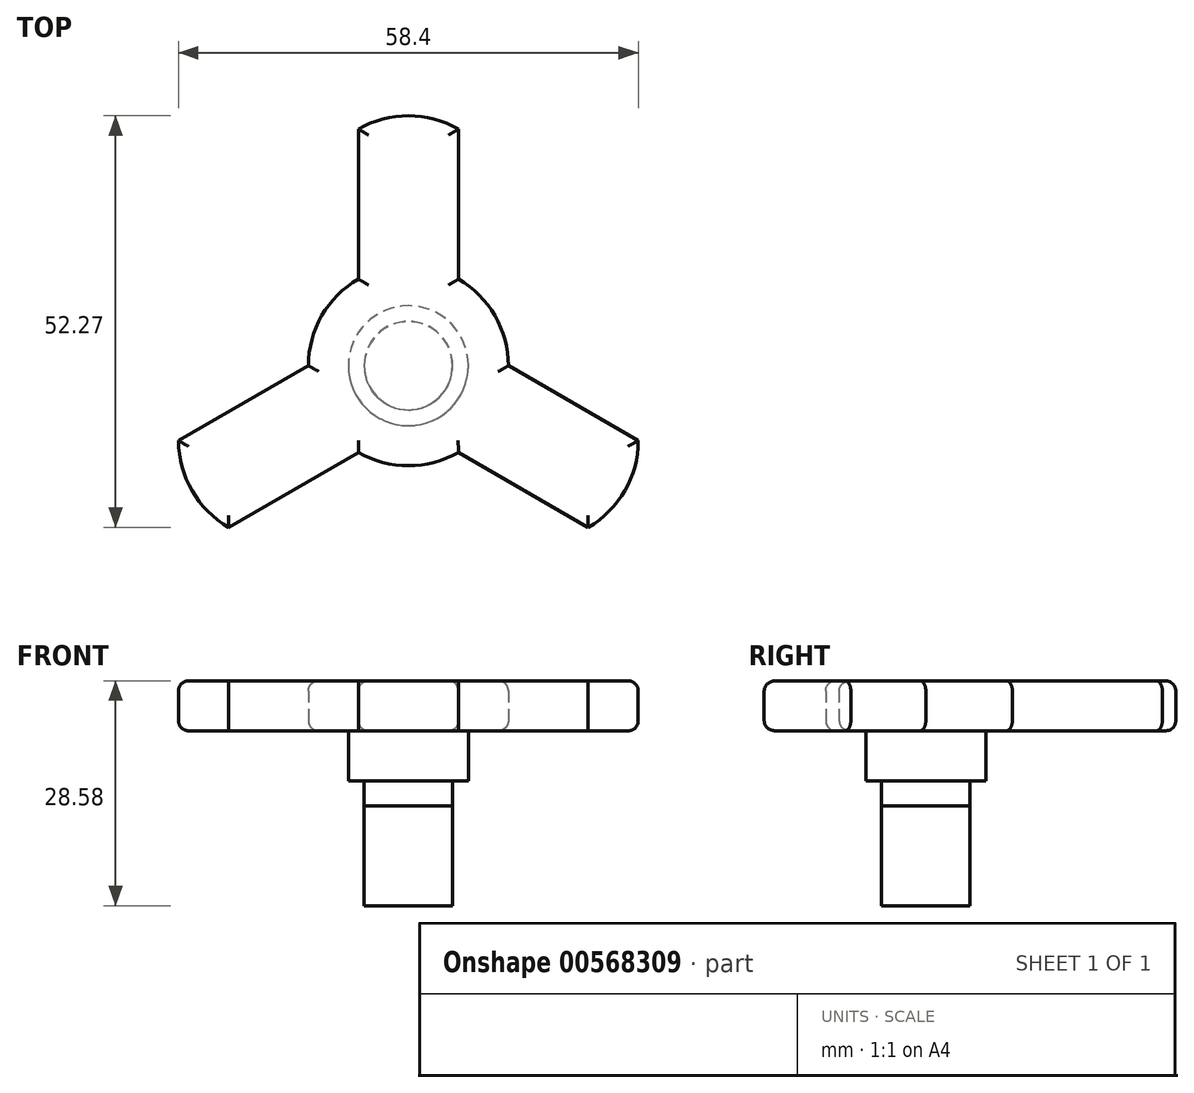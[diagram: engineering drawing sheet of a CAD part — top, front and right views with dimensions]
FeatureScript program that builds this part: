
annotation { "Feature Type Name" : "Feature", "Feature Type Description" : "" }
export const myFeature = defineFeature(function(context is Context, id is Id, definition is map)
    precondition{}
    {
        {
            var Q0;
            Q0=qCreatedBy(makeId("Top.planeOp"),FACE);
            var sketch = newSketch(context, id + "F0", { "sketchPlane" : qUnion([Q0])});
            skCircle(sketch, "E0", {"center": v(0, 0) * mm, "radius": 5.63 * mm});
            skSolve(sketch);
        }
        {
            var Q0;
            Q0 = qSketchRegion(id + "F0", true);
            extrude(context, id + "F1", {"entities" : qUnion([Q0]), "depth" : 12.7 * mm, "offsetDistance" : 25.4 * mm});
        }
        {
            var Q0;
            Q0=makeQuery(id+"F1.opExtrude","CAP_FACE",FACE,{"disambiguationData":[OSD([sQuery(id+"F0.wireOp",EDGE,"E0")])],"isStart":false});
            var sketch = newSketch(context, id + "F2", { "sketchPlane" : qUnion([Q0])});
            skCircle(sketch, "E1", {"center": v(0, 0) * mm, "radius": 5.6 * mm});
            skSolve(sketch);
        }
        {
            var Q0;
            Q0 = qSketchRegion(id + "F2", true);
            extrude(context, id + "F3", {"entities" : qUnion([Q0]), "operationType" : NewBodyOperationType.ADD, "depth" : 9.52 * mm, "offsetDistance" : 25.4 * mm});
        }
        {
            var Q0;
            Q0=makeQuery(id+"F3.opExtrude","CAP_FACE",FACE,{"disambiguationData":[OSD([sQuery(id+"F2.wireOp",EDGE,"E1")])],"isStart":false});
            var sketch = newSketch(context, id + "F4", { "sketchPlane" : qUnion([Q0])});
            skCircle(sketch, "E2", {"center": v(0, 0) * mm, "radius": 12.7 * mm});
            skSolve(sketch);
        }
        {
            var Q0;
            Q0=makeQuery(id+"F4.imprint","IMPRINT",FACE,{"disambiguationData":[TD([[makeQuery(id+"F4.imprint","IMPRINT",EDGE,{"derivedFrom":sQuery(id+"F4.wireOp",EDGE,"E2")}),1.0]])]});
            var sketch = newSketch(context, id + "F5", { "sketchPlane" : qUnion([Q0])});
            skLineSegment(sketch, "E3.left", {"start": v(-6.35, 11) * mm, "end": v(-6.35, 30.05) * mm});
            skLineSegment(sketch, "E3.right", {"start": v(6.35, 11) * mm, "end": v(6.35, 30.05) * mm});
            skLineSegment(sketch, "E4.1.0", {"start": v(-12.7, 0) * mm, "end": v(-29.2, -9.52) * mm});
            skLineSegment(sketch, "E4.2.0", {"start": v(6.35, -11) * mm, "end": v(22.85, -20.52) * mm});
            skPoint(sketch, "E4.center", {"position": v(0, 0) * mm});
            skLineSegment(sketch, "E5.1.0", {"start": v(-6.35, -11) * mm, "end": v(-22.85, -20.52) * mm});
            skLineSegment(sketch, "E5.2.0", {"start": v(12.7, 0) * mm, "end": v(29.2, -9.52) * mm});
            skArc(sketch, "E6", {"start": v(6.35, 30.05) * mm, "mid": v(0, 31.75) * mm, "end": v(-6.35, 30.05) * mm});
            skArc(sketch, "E7.1.0", {"start": v(-29.2, -9.52) * mm, "mid": v(-27.5, -15.87) * mm, "end": v(-22.85, -20.52) * mm});
            skArc(sketch, "E7.2.0", {"start": v(22.85, -20.52) * mm, "mid": v(27.5, -15.87) * mm, "end": v(29.2, -9.52) * mm});
            skSolve(sketch);
        }
        {
            var Q0;
            Q0=makeQuery(id+"F4.imprint","IMPRINT",FACE,{"disambiguationData":[TD([[makeQuery(id+"F4.imprint","IMPRINT",EDGE,{"derivedFrom":sQuery(id+"F4.wireOp",EDGE,"E2")}),1.0]])]});
            extrude(context, id + "F6", {"entities" : qUnion([Q0]), "operationType" : NewBodyOperationType.ADD, "depth" : 6.35 * mm, "offsetDistance" : 25.4 * mm});
        }
        {
            var Q0;
            Q0=makeQuery(id+"F3.opExtrude","CAP_FACE",FACE,{"disambiguationData":[OSD([sQuery(id+"F2.wireOp",EDGE,"E1")])],"isStart":false});
            extrude(context, id + "F7", {"entities" : qUnion([Q0]), "operationType" : NewBodyOperationType.ADD, "depth" : 6.35 * mm, "offsetDistance" : 25.4 * mm});
        }
        {
            var Q0;
            Q0=makeQuery(id+"F6.opExtrude","CAP_FACE",FACE,{"disambiguationData":[OSD([sQuery(id+"F2.wireOp",EDGE,"E1"),sQuery(id+"F4.wireOp",EDGE,"E2")])],"isStart":true});
            var sketch = newSketch(context, id + "F8", { "sketchPlane" : qUnion([Q0])});
            skCircle(sketch, "E8", {"center": v(0, 0) * mm, "radius": 7.62 * mm});
            skSolve(sketch);
        }
        {
            var Q0;
            Q0 = qSketchRegion(id + "F8", true);
            extrude(context, id + "F9", {"entities" : qUnion([Q0]), "operationType" : NewBodyOperationType.ADD, "depth" : 6.35 * mm, "offsetDistance" : 25.4 * mm});
        }
        {
            var Q0;
            {var subQ0=sQuery(id+"F5.wireOp",EDGE,"E7.1.0");Q0=makeQuery(id+"F5.imprint","IMPRINT",FACE,{"disambiguationData":[TD([[makeQuery(id+"F5.imprint","IMPRINT",EDGE,{"derivedFrom":subQ0}),1.0]])]});}
            var Q1;
            {var subQ0=sQuery(id+"F5.wireOp",EDGE,"E6");Q1=makeQuery(id+"F5.imprint","IMPRINT",FACE,{"disambiguationData":[TD([[makeQuery(id+"F5.imprint","IMPRINT",EDGE,{"derivedFrom":subQ0}),1.0]])]});}
            var Q2;
            {var subQ0=sQuery(id+"F5.wireOp",EDGE,"E7.2.0");Q2=makeQuery(id+"F5.imprint","IMPRINT",FACE,{"disambiguationData":[TD([[makeQuery(id+"F5.imprint","IMPRINT",EDGE,{"derivedFrom":subQ0}),1.0]])]});}
            extrude(context, id + "F10", {"entities" : qUnion([Q0, Q1, Q2]), "operationType" : NewBodyOperationType.ADD, "depth" : 6.35 * mm, "offsetDistance" : 25.4 * mm});
        }
        {
            var Q0;
            Q0=makeQuery(id+"F10.opExtrude","CAP_EDGE",EDGE,{"disambiguationData":[OSD([sQuery(id+"F5.wireOp",EDGE,"E3.right")])],"isStart":false});
            var Q1;
            Q1=makeQuery(id+"F10.opExtrude","CAP_EDGE",EDGE,{"disambiguationData":[OSD([sQuery(id+"F5.wireOp",EDGE,"E5.2.0")])],"isStart":false});
            var Q2;
            Q2=makeQuery(id+"F10.opExtrude","CAP_EDGE",EDGE,{"disambiguationData":[OSD([sQuery(id+"F5.wireOp",EDGE,"E7.2.0")])],"isStart":false});
            var Q3;
            Q3=makeQuery(id+"F10.opExtrude","CAP_EDGE",EDGE,{"disambiguationData":[OSD([sQuery(id+"F5.wireOp",EDGE,"E4.2.0")])],"isStart":false});
            var Q4;
            Q4=makeQuery(id+"F10.opExtrude","CAP_EDGE",EDGE,{"disambiguationData":[OSD([sQuery(id+"F5.wireOp",EDGE,"E6")])],"isStart":false});
            var Q5;
            Q5=makeQuery(id+"F10.opExtrude","CAP_EDGE",EDGE,{"disambiguationData":[OSD([sQuery(id+"F5.wireOp",EDGE,"E3.left")])],"isStart":false});
            var Q6;
            Q6=makeQuery(id+"F10.opExtrude","CAP_EDGE",EDGE,{"disambiguationData":[OSD([sQuery(id+"F5.wireOp",EDGE,"E4.1.0")])],"isStart":false});
            var Q7;
            Q7=makeQuery(id+"F10.opExtrude","CAP_EDGE",EDGE,{"disambiguationData":[OSD([sQuery(id+"F5.wireOp",EDGE,"E5.1.0")])],"isStart":false});
            var Q8;
            Q8=makeQuery(id+"F10.opExtrude","CAP_EDGE",EDGE,{"disambiguationData":[OSD([sQuery(id+"F5.wireOp",EDGE,"E7.1.0")])],"isStart":false});
            var Q9;
            Q9=makeQuery(id+"F10.opExtrude","CAP_EDGE",EDGE,{"disambiguationData":[OSD([sQuery(id+"F5.wireOp",EDGE,"E7.1.0")])],"isStart":true});
            var Q10;
            Q10=makeQuery(id+"F10.opExtrude","CAP_EDGE",EDGE,{"disambiguationData":[OSD([sQuery(id+"F5.wireOp",EDGE,"E4.1.0")])],"isStart":true});
            var Q11;
            Q11=makeQuery(id+"F10.opExtrude","CAP_EDGE",EDGE,{"disambiguationData":[OSD([sQuery(id+"F5.wireOp",EDGE,"E3.left")])],"isStart":true});
            var Q12;
            Q12=makeQuery(id+"F10.opExtrude","CAP_EDGE",EDGE,{"disambiguationData":[OSD([sQuery(id+"F5.wireOp",EDGE,"E6")])],"isStart":true});
            var Q13;
            Q13=makeQuery(id+"F10.opExtrude","CAP_EDGE",EDGE,{"disambiguationData":[OSD([sQuery(id+"F5.wireOp",EDGE,"E3.right")])],"isStart":true});
            var Q14;
            Q14=makeQuery(id+"F10.opExtrude","CAP_EDGE",EDGE,{"disambiguationData":[OSD([sQuery(id+"F5.wireOp",EDGE,"E5.2.0")])],"isStart":true});
            var Q15;
            Q15=makeQuery(id+"F10.opExtrude","CAP_EDGE",EDGE,{"disambiguationData":[OSD([sQuery(id+"F5.wireOp",EDGE,"E7.2.0")])],"isStart":true});
            var Q16;
            Q16=makeQuery(id+"F10.opExtrude","CAP_EDGE",EDGE,{"disambiguationData":[OSD([sQuery(id+"F5.wireOp",EDGE,"E4.2.0")])],"isStart":true});
            var Q17;
            Q17=makeQuery(id+"F10.opExtrude","CAP_EDGE",EDGE,{"disambiguationData":[OSD([sQuery(id+"F5.wireOp",EDGE,"E5.1.0")])],"isStart":true});
            var Q18;
            {var subQ0=sQuery(id+"F5.wireOp",EDGE,"E3.left");var subQ2=sQuery(id+"F4.wireOp",EDGE,"E2");Q18=makeQuery(id+"F10.boolean.opBoolean","SPLIT",EDGE,{"disambiguationData":[TD([makeQuery(id+"F10.opExtrude","SWEPT_FACE",FACE,{"disambiguationData":[OSD([subQ0])]})])],"derivedFrom":makeQuery(id+"F6.opExtrude","CAP_EDGE",EDGE,{"disambiguationData":[OSD([subQ2])],"isStart":true})});}
            var Q19;
            {var subQ1=sQuery(id+"F4.wireOp",EDGE,"E2");var subQ2=sQuery(id+"F5.wireOp",EDGE,"E4.2.0");Q19=makeQuery(id+"F10.boolean.opBoolean","SPLIT",EDGE,{"disambiguationData":[TD([makeQuery(id+"F10.opExtrude","SWEPT_FACE",FACE,{"disambiguationData":[OSD([subQ2])]})])],"derivedFrom":makeQuery(id+"F6.opExtrude","CAP_EDGE",EDGE,{"disambiguationData":[OSD([subQ1])],"isStart":true})});}
            var Q20;
            {var subQ1=sQuery(id+"F4.wireOp",EDGE,"E2");var subQ2=sQuery(id+"F5.wireOp",EDGE,"E3.right");Q20=makeQuery(id+"F10.boolean.opBoolean","SPLIT",EDGE,{"disambiguationData":[TD([makeQuery(id+"F10.opExtrude","SWEPT_FACE",FACE,{"disambiguationData":[OSD([subQ2])]})])],"derivedFrom":makeQuery(id+"F6.opExtrude","CAP_EDGE",EDGE,{"disambiguationData":[OSD([subQ1])],"isStart":true})});}
            var Q21;
            {var subQ0=sQuery(id+"F5.wireOp",EDGE,"E3.right");var subQ1=sQuery(id+"F4.wireOp",EDGE,"E2");Q21=makeQuery(id+"F10.boolean.opBoolean","SPLIT",EDGE,{"disambiguationData":[TD([makeQuery(id+"F10.opExtrude","SWEPT_FACE",FACE,{"disambiguationData":[OSD([subQ0])]})])],"derivedFrom":makeQuery(id+"F6.opExtrude","CAP_EDGE",EDGE,{"disambiguationData":[OSD([subQ1])],"isStart":false})});}
            var Q22;
            {var subQ0=sQuery(id+"F5.wireOp",EDGE,"E3.left");var subQ2=sQuery(id+"F4.wireOp",EDGE,"E2");Q22=makeQuery(id+"F10.boolean.opBoolean","SPLIT",EDGE,{"disambiguationData":[TD([makeQuery(id+"F10.opExtrude","SWEPT_FACE",FACE,{"disambiguationData":[OSD([subQ0])]})])],"derivedFrom":makeQuery(id+"F6.opExtrude","CAP_EDGE",EDGE,{"disambiguationData":[OSD([subQ2])],"isStart":false})});}
            var Q23;
            {var subQ0=sQuery(id+"F4.wireOp",EDGE,"E2");var subQ3=sQuery(id+"F5.wireOp",EDGE,"E4.2.0");Q23=makeQuery(id+"F10.boolean.opBoolean","SPLIT",EDGE,{"disambiguationData":[TD([makeQuery(id+"F10.opExtrude","SWEPT_FACE",FACE,{"disambiguationData":[OSD([subQ3])]})])],"derivedFrom":makeQuery(id+"F6.opExtrude","CAP_EDGE",EDGE,{"disambiguationData":[OSD([subQ0])],"isStart":false})});}
            fillet(context, id + "F11", {"entities" : qUnion([Q0, Q1, Q2, Q3, Q4, Q5, Q6, Q7, Q8, Q9, Q10, Q11, Q12, Q13, Q14, Q15, Q16, Q17, Q18, Q19, Q20, Q21, Q22, Q23]), "radius" : 1.27 * mm, "tangentPropagation" : true, "allowEdgeOverflow" : false});
        }
    });
